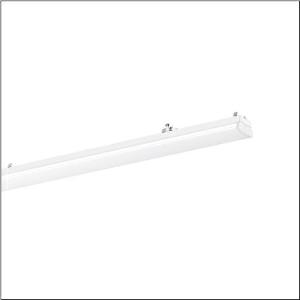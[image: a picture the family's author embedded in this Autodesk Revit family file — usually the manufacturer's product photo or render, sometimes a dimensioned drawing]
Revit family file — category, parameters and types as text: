
# Revit family: licross_r__11_recessed_opal_ho_51tl1ddn46xm_4fcf
name_source: partatom
category: Lighting Fixtures
units: mm (PartAtom-declared; Revit-internal decimal feet)

## family parameters
Cut with Voids When Loaded = No
Host = Face
Light Source = No
Part Type = Normal
Room Calculation Point = No
Round Connector Dimension = Use Diameter
Shared = No

## types (1)
- --- (1 x LED, 6320 lm, 33.5 W, 4000K)
    Apparent Load = 34 VA
    CIE Flux Codes = 44 73 91 87 100
    Color Rendering = 80
    Color Temperature = 4000K
    Default Elevation = 1800 mm
    Description = Licross® 11 recessed opal HO, luminaire insert, of sheet steel, coil coated, white, length: 1.500mm, width: 76mm, height: 87mm, LED rated luminous flux: 6.320lm, light colour: 840, control gear: DALI 2, with plug, 5-pole, with phase selection, mains connection: 220..240V, AC, 50/60Hz, rated input power: 34W, halogen-free wiring, primary optical cover: cover, of PMMA, light emission: direct with ceiling illumination distribution, primary light characteristic: symmetric, protection rating (complete): IP40, insulation class (complete): insulation class I (protective earthing), certification: CE, ENEC, VDE, UKCA, protection symbol: D if used in an environment without relevant dust loads with corresponding accessories, impact resistance: IK06, permissible ambient temperature for indoor applications: -25..+45°C, corresponds to IFS (International Featured Standards) requirements for safety and quality in the food industry, reducing of maximum allowable ambient temperature of 5°C with ceiling mounting, LABS conformity tested according to VDMA 24364:2018-05, packaging unit: 1 piece
    Height = 83 mm
    Lamp = 1 x LED
    Lamp Light Flux = 6320 lm
    Lamp Power = 33.5 W
    Lamp count = 1
    Length = 1500 mm
    Luminous efficacy = 189 lm/W
    Manufacturer = Siteco
    ModVariant = No
    Model = 51TL1DDN46XM
    Mounting Place = Ceiling
    Mounting Type = Pendant
    Number of Poles = 1
    OnlyDefault = Yes
    Power Factor = 1
    Product Name = Licross® 11 recessed opal HO
    Product group = luminaire insert
    ProductGroupID = 901
    Protection Class = Protection class I
    Protection Degree = IP 40
    RLX_Detail_Level = 1
    RLX_Emergency_Light_Flux = 0 lm
    RLX_Emergency_Type = 0
    RLX_Emergency_Type_DB = No
    RlxData = <blob elided: 26661 chars, md5=71b06df8>
    Socket = socket
    Standby Power = 0 W
    System Light Flux = 6320 lm
    System Power = 34 W
    Type Comments = factory setting: luminous flux: 100 % | dim-lin: 254 | 232 mA
    Type Image = l_1313666.jpg
    URL = http://relux.com
    VarID = @adj_045087
    Voltage = 0 V
    Weight = 0.00 kg
    Width = 76 mm

## geometry (parser evidence)
native form markers: Blend x4, Sweep x12
no freeform markers — native parametric forms only
